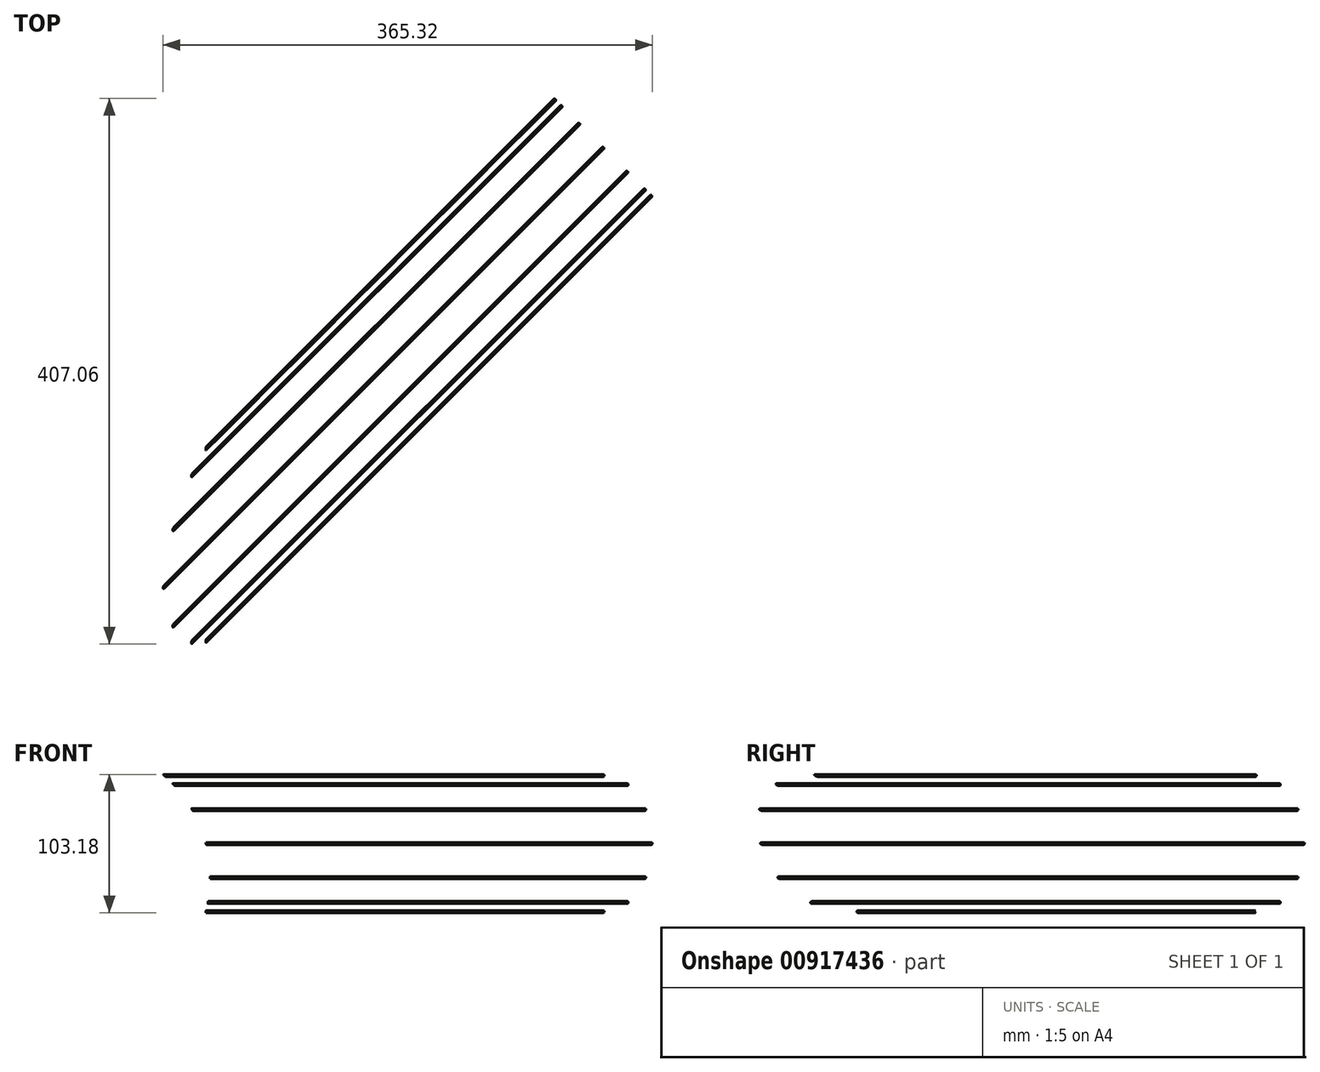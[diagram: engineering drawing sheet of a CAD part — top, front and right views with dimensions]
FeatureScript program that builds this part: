
annotation { "Feature Type Name" : "Feature", "Feature Type Description" : "" }
export const myFeature = defineFeature(function(context is Context, id is Id, definition is map)
    precondition{}
    {
        {
            var Q0;
            Q0=qCreatedBy(makeId("Front.planeOp"),FACE);
            var sketch = newSketch(context, id + "F0", { "sketchPlane" : qUnion([Q0])});
            skArc(sketch, "E0", {"start": v(-0.13, 101.6) * mm, "mid": v(0, -101.6) * mm, "end": v(0.13, 101.6) * mm});
            skLineSegment(sketch, "E1", {"start": v(-0.13, 101.6) * mm, "end": v(0.13, 101.6) * mm, "construction": true});
            skLineSegment(sketch, "E2", {"start": v(0, 101.6) * mm, "end": v(0, 0) * mm, "construction": true});
            skSolve(sketch);
        }
        {
            var Q0;
            Q0 = qSketchRegion(id + "F0", true);
            var Q1;
            Q1=sQuery(id+"F0.wireOp",EDGE,"E0");
            extrude(context, id + "F1", {"entities" : qUnion([Q0]), "bodyType" : ToolBodyType.SURFACE, "surfaceEntities" : qUnion([Q1]), "depth" : 609.6 * mm, "offsetDistance" : 25.4 * mm});
        }
        {
            var Q0;
            Q0=qCreatedBy(makeId("Top.planeOp"),FACE);
            cPlane(context, id + "F2", {"entities" : qUnion([Q0]), "cplaneType" : CPlaneType.OFFSET, "offset" : 25.4 * mm, "width" : 152.4 * mm, "height" : 152.4 * mm});
        }
        {
            var Q0;
            Q0=qCreatedBy(id+"F2.planeOp",FACE);
            var sketch = newSketch(context, id + "F3", { "sketchPlane" : qUnion([Q0])});
            skLineSegment(sketch, "E3", {"start": v(0.56, -305.36) * mm, "end": v(431.61, 125.7) * mm});
            skLineSegment(sketch, "E4", {"start": v(431.61, 125.7) * mm, "end": v(431.05, 126.25) * mm});
            skLineSegment(sketch, "E5", {"start": v(431.05, 126.25) * mm, "end": v(0, -304.8) * mm});
            skLineSegment(sketch, "E6", {"start": v(0, -304.8) * mm, "end": v(0.56, -305.36) * mm});
            skLineSegment(sketch, "E7", {"start": v(0, 0) * mm, "end": v(0, -605.6) * mm, "construction": true});
            skLineSegment(sketch, "E8", {"start": v(0, -304.8) * mm, "end": v(-35.92, -268.88) * mm, "construction": true});
            skLineSegment(sketch, "E9", {"start": v(-35.92, -268.88) * mm, "end": v(395.13, 162.17) * mm, "construction": true});
            skSolve(sketch);
        }
        {
            var Q0;
            Q0 = qSketchRegion(id + "F3", true);
            var Q1;
            Q1=sQuery(id+"F3.wireOp",EDGE,"E5");
            revolve(context, id + "F4", {"surfaceOperationType" : NewSurfaceOperationType.NEW, "entities" : qUnion([Q0]), "axis" : qUnion([Q1]), "revolveType" : RevolveType.FULL});
        }
        {
            var Q0;
            Q0=makeQuery(id+"F4.opRevolve","SWEPT_BODY",BODY,{"disambiguationData":[OSD([sQuery(id+"F3.wireOp",EDGE,"E3"),sQuery(id+"F3.wireOp",EDGE,"E4"),sQuery(id+"F3.wireOp",EDGE,"E5"),sQuery(id+"F3.wireOp",EDGE,"E6")])]});
            var Q1;
            Q1=sQuery(id+"F3.wireOp",EDGE,"E9");
            circularPattern(context, id + "F5", {"entities" : qUnion([Q0]), "axis" : qUnion([Q1]), "angle" : 360 * degree, "instanceCount" : 12, "equalSpace" : true});
        }
        {
            var Q0;
            Q0=qCreatedBy(makeId("Front.planeOp"),FACE);
            var sketch = newSketch(context, id + "F6", { "sketchPlane" : qUnion([Q0])});
            skCircle(sketch, "E10", {"center": v(0, 0) * mm, "radius": 101.6 * mm});
            skSolve(sketch);
        }
        {
            var Q0;
            Q0 = qSketchRegion(id + "F6", true);
            extrude(context, id + "F7", {"entities" : qUnion([Q0]), "operationType" : NewBodyOperationType.REMOVE, "endBound" : BoundingType.THROUGH_ALL, "depth" : 25.4 * mm, "offsetDistance" : 25.4 * mm});
        }
    });
